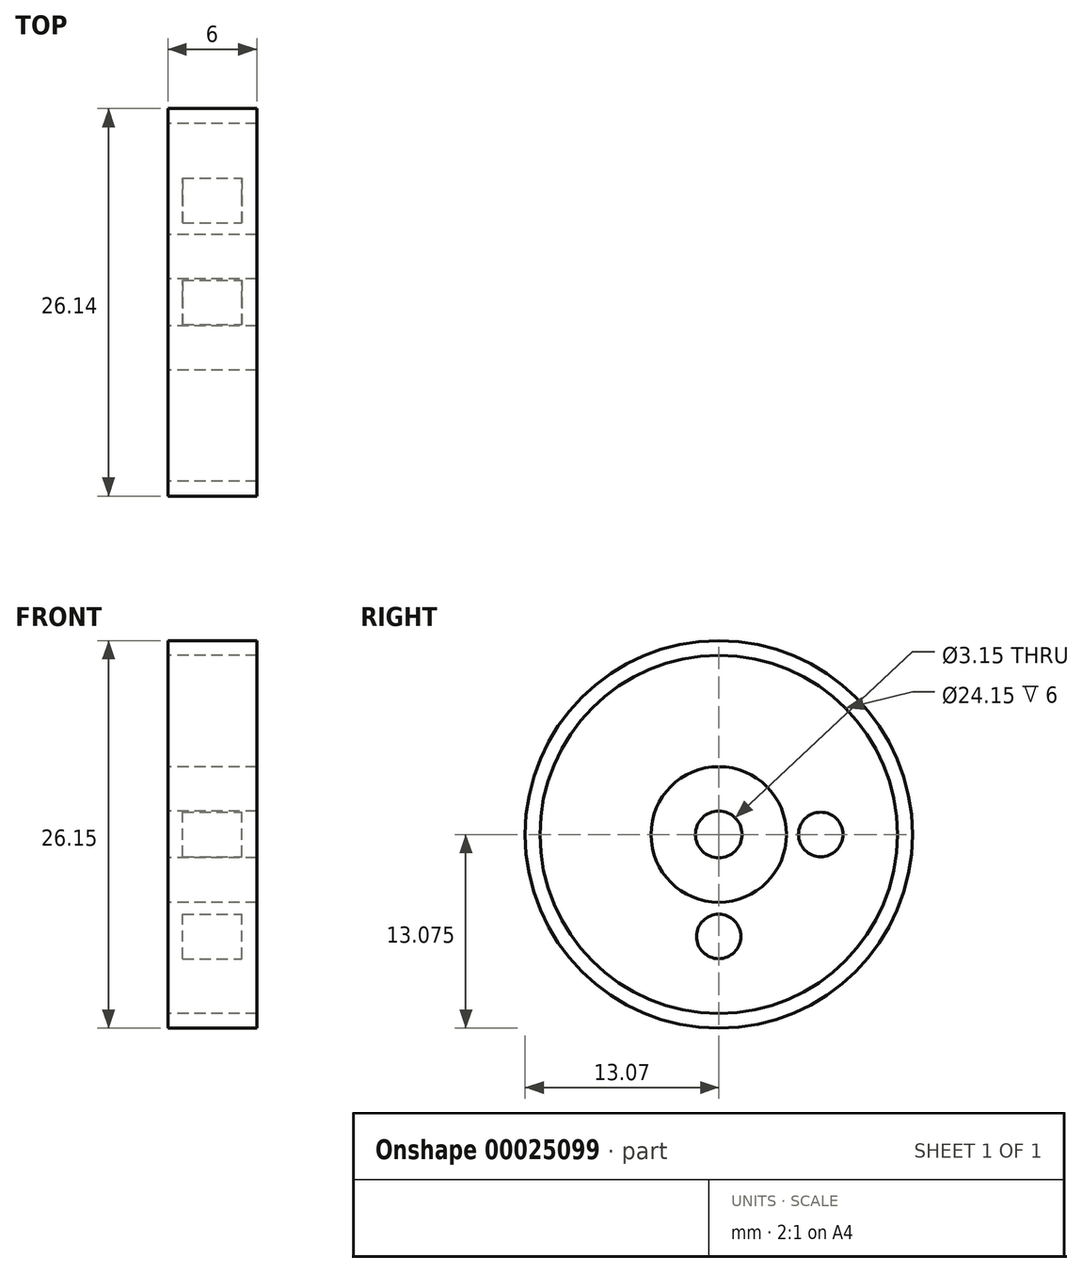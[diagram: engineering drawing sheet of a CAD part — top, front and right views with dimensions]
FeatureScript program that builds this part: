
annotation { "Feature Type Name" : "Feature", "Feature Type Description" : "" }
export const myFeature = defineFeature(function(context is Context, id is Id, definition is map)
    precondition{}
    {
        {
            var Q0;
            Q0=qCreatedBy(makeId("Front.planeOp"),FACE);
            var sketch = newSketch(context, id + "F0", { "sketchPlane" : qUnion([Q0])});
            skLineSegment(sketch, "E0.bottom", {"start": v(-0.12, 1.48) * mm, "end": v(0.88, 1.48) * mm});
            skLineSegment(sketch, "E0.top", {"start": v(-0.12, -1.52) * mm, "end": v(5.88, -1.52) * mm});
            skLineSegment(sketch, "E0.left", {"start": v(-0.12, 1.48) * mm, "end": v(-0.12, -1.52) * mm});
            skLineSegment(sketch, "E0.right", {"start": v(5.88, 1.48) * mm, "end": v(5.88, -1.52) * mm});
            skLineSegment(sketch, "E1.left", {"start": v(0.88, 8.98) * mm, "end": v(0.88, 1.48) * mm});
            skLineSegment(sketch, "E1.right", {"start": v(4.88, 8.98) * mm, "end": v(4.88, 1.48) * mm});
            skLineSegment(sketch, "E2.trimOffspring", {"start": v(4.88, 1.48) * mm, "end": v(5.88, 1.48) * mm});
            skLineSegment(sketch, "E3", {"start": v(-11.4, -3.1) * mm, "end": v(19.97, -3.1) * mm, "construction": true});
            skLineSegment(sketch, "E4.bottom", {"start": v(5.88, 9.98) * mm, "end": v(-0.12, 9.98) * mm});
            skLineSegment(sketch, "E4.top", {"start": v(5.88, 8.98) * mm, "end": v(4.88, 8.98) * mm});
            skLineSegment(sketch, "E4.left", {"start": v(5.88, 9.98) * mm, "end": v(5.88, 8.98) * mm});
            skLineSegment(sketch, "E4.right", {"start": v(-0.12, 9.98) * mm, "end": v(-0.12, 8.98) * mm});
            skLineSegment(sketch, "E5.trimOffspring", {"start": v(0.88, 8.98) * mm, "end": v(-0.12, 8.98) * mm});
            skSolve(sketch);
        }
        {
            var Q0;
            Q0 = qSketchRegion(id + "F0", true);
            var Q1;
            Q1=sQuery(id+"F0.wireOp",EDGE,"E3");
            revolve(context, id + "F1", {"entities" : qUnion([Q0]), "axis" : qUnion([Q1]), "revolveType" : RevolveType.FULL});
        }
        {
            var Q0;
            Q0=makeQuery(id+"F1.opRevolve","SWEPT_FACE",FACE,{"disambiguationData":[OSD([sQuery(id+"F0.wireOp",EDGE,"E1.right")])]});
            var sketch = newSketch(context, id + "F2", { "sketchPlane" : qUnion([Q0])});
            skCircle(sketch, "E6", {"center": v(0, -3.1) * mm, "radius": 6.88 * mm});
            skCircle(sketch, "E7", {"center": v(0, -9.98) * mm, "radius": 1.5 * mm});
            skCircle(sketch, "E8.1.0", {"center": v(4.87, -7.96) * mm, "radius": 1.5 * mm});
            skCircle(sketch, "E8.2.0", {"center": v(6.88, -3.1) * mm, "radius": 1.5 * mm});
            skCircle(sketch, "E8.3.0", {"center": v(4.87, 1.77) * mm, "radius": 1.5 * mm});
            skCircle(sketch, "E8.4.0", {"center": v(0, 3.79) * mm, "radius": 1.5 * mm});
            skCircle(sketch, "E8.5.0", {"center": v(-4.87, 1.77) * mm, "radius": 1.5 * mm});
            skCircle(sketch, "E8.6.0", {"center": v(-6.88, -3.1) * mm, "radius": 1.5 * mm});
            skCircle(sketch, "E8.7.0", {"center": v(-4.87, -7.96) * mm, "radius": 1.5 * mm});
            skSolve(sketch);
        }
        {
            var Q0;
            {var subQ0=sQuery(id+"F2.wireOp",EDGE,"E8.5.0");var subQ1=sQuery(id+"F2.wireOp",EDGE,"E6");var subQ3=makeQuery(id+"F2.imprint","INTERSECT",VERTEX,{"disambiguationData":[OD(0.0)],"derivedFrom":[subQ1,subQ0]});Q0=makeQuery(id+"F2.imprint","IMPRINT",FACE,{"disambiguationData":[TD([[makeQuery(id+"F2.imprint","IMPRINT",EDGE,{"disambiguationData":[TD([[subQ3,-1.0]])],"derivedFrom":subQ1}),1.0]])]});}
            var Q1;
            {var subQ0=sQuery(id+"F2.wireOp",EDGE,"E8.5.0");var subQ1=sQuery(id+"F2.wireOp",EDGE,"E6");var subQ3=makeQuery(id+"F2.imprint","INTERSECT",VERTEX,{"disambiguationData":[OD(0.0)],"derivedFrom":[subQ1,subQ0]});Q1=makeQuery(id+"F2.imprint","IMPRINT",FACE,{"disambiguationData":[TD([[makeQuery(id+"F2.imprint","IMPRINT",EDGE,{"disambiguationData":[TD([[subQ3,-1.0]])],"derivedFrom":subQ1}),-1.0]])]});}
            var Q2;
            {var subQ0=sQuery(id+"F2.wireOp",EDGE,"E8.6.0");var subQ1=sQuery(id+"F2.wireOp",EDGE,"E6");var subQ3=makeQuery(id+"F2.imprint","INTERSECT",VERTEX,{"disambiguationData":[OD(0.0)],"derivedFrom":[subQ1,subQ0]});Q2=makeQuery(id+"F2.imprint","IMPRINT",FACE,{"disambiguationData":[TD([[makeQuery(id+"F2.imprint","IMPRINT",EDGE,{"disambiguationData":[TD([[subQ3,-1.0]])],"derivedFrom":subQ1}),1.0]])]});}
            var Q3;
            {var subQ0=sQuery(id+"F2.wireOp",EDGE,"E8.6.0");var subQ1=sQuery(id+"F2.wireOp",EDGE,"E6");var subQ3=makeQuery(id+"F2.imprint","INTERSECT",VERTEX,{"disambiguationData":[OD(0.0)],"derivedFrom":[subQ1,subQ0]});Q3=makeQuery(id+"F2.imprint","IMPRINT",FACE,{"disambiguationData":[TD([[makeQuery(id+"F2.imprint","IMPRINT",EDGE,{"disambiguationData":[TD([[subQ3,-1.0]])],"derivedFrom":subQ1}),-1.0]])]});}
            var Q4;
            {var subQ0=sQuery(id+"F2.wireOp",EDGE,"E8.7.0");var subQ1=sQuery(id+"F2.wireOp",EDGE,"E6");var subQ3=makeQuery(id+"F2.imprint","INTERSECT",VERTEX,{"disambiguationData":[OD(0.0)],"derivedFrom":[subQ1,subQ0]});Q4=makeQuery(id+"F2.imprint","IMPRINT",FACE,{"disambiguationData":[TD([[makeQuery(id+"F2.imprint","IMPRINT",EDGE,{"disambiguationData":[TD([[subQ3,-1.0]])],"derivedFrom":subQ1}),1.0]])]});}
            var Q5;
            {var subQ0=sQuery(id+"F2.wireOp",EDGE,"E8.7.0");var subQ1=sQuery(id+"F2.wireOp",EDGE,"E6");var subQ3=makeQuery(id+"F2.imprint","INTERSECT",VERTEX,{"disambiguationData":[OD(0.0)],"derivedFrom":[subQ1,subQ0]});Q5=makeQuery(id+"F2.imprint","IMPRINT",FACE,{"disambiguationData":[TD([[makeQuery(id+"F2.imprint","IMPRINT",EDGE,{"disambiguationData":[TD([[subQ3,-1.0]])],"derivedFrom":subQ1}),-1.0]])]});}
            var Q6;
            {var subQ0=sQuery(id+"F2.wireOp",EDGE,"E7");var subQ1=sQuery(id+"F2.wireOp",EDGE,"E6");var subQ3=makeQuery(id+"F2.imprint","INTERSECT",VERTEX,{"disambiguationData":[OD(0.0)],"derivedFrom":[subQ1,subQ0]});Q6=makeQuery(id+"F2.imprint","IMPRINT",FACE,{"disambiguationData":[TD([[makeQuery(id+"F2.imprint","IMPRINT",EDGE,{"disambiguationData":[TD([[subQ3,-1.0]])],"derivedFrom":subQ1}),1.0]])]});}
            var Q7;
            {var subQ0=sQuery(id+"F2.wireOp",EDGE,"E7");var subQ1=sQuery(id+"F2.wireOp",EDGE,"E6");var subQ3=makeQuery(id+"F2.imprint","INTERSECT",VERTEX,{"disambiguationData":[OD(0.0)],"derivedFrom":[subQ1,subQ0]});Q7=makeQuery(id+"F2.imprint","IMPRINT",FACE,{"disambiguationData":[TD([[makeQuery(id+"F2.imprint","IMPRINT",EDGE,{"disambiguationData":[TD([[subQ3,-1.0]])],"derivedFrom":subQ1}),-1.0]])]});}
            var Q8;
            {var subQ0=sQuery(id+"F2.wireOp",EDGE,"E8.1.0");var subQ1=sQuery(id+"F2.wireOp",EDGE,"E6");var subQ3=makeQuery(id+"F2.imprint","INTERSECT",VERTEX,{"disambiguationData":[OD(0.0)],"derivedFrom":[subQ1,subQ0]});Q8=makeQuery(id+"F2.imprint","IMPRINT",FACE,{"disambiguationData":[TD([[makeQuery(id+"F2.imprint","IMPRINT",EDGE,{"disambiguationData":[TD([[subQ3,-1.0]])],"derivedFrom":subQ1}),1.0]])]});}
            var Q9;
            {var subQ0=sQuery(id+"F2.wireOp",EDGE,"E8.1.0");var subQ1=sQuery(id+"F2.wireOp",EDGE,"E6");var subQ3=makeQuery(id+"F2.imprint","INTERSECT",VERTEX,{"disambiguationData":[OD(0.0)],"derivedFrom":[subQ1,subQ0]});Q9=makeQuery(id+"F2.imprint","IMPRINT",FACE,{"disambiguationData":[TD([[makeQuery(id+"F2.imprint","IMPRINT",EDGE,{"disambiguationData":[TD([[subQ3,-1.0]])],"derivedFrom":subQ1}),-1.0]])]});}
            var Q10;
            {var subQ0=sQuery(id+"F2.wireOp",EDGE,"E8.2.0");var subQ1=sQuery(id+"F2.wireOp",EDGE,"E6");var subQ3=makeQuery(id+"F2.imprint","INTERSECT",VERTEX,{"disambiguationData":[OD(0.0)],"derivedFrom":[subQ1,subQ0]});Q10=makeQuery(id+"F2.imprint","IMPRINT",FACE,{"disambiguationData":[TD([[makeQuery(id+"F2.imprint","IMPRINT",EDGE,{"disambiguationData":[TD([[subQ3,1.0]])],"derivedFrom":subQ1}),1.0]])]});}
            var Q11;
            {var subQ0=sQuery(id+"F2.wireOp",EDGE,"E8.2.0");var subQ1=sQuery(id+"F2.wireOp",EDGE,"E6");var subQ3=makeQuery(id+"F2.imprint","INTERSECT",VERTEX,{"disambiguationData":[OD(0.0)],"derivedFrom":[subQ1,subQ0]});Q11=makeQuery(id+"F2.imprint","IMPRINT",FACE,{"disambiguationData":[TD([[makeQuery(id+"F2.imprint","IMPRINT",EDGE,{"disambiguationData":[TD([[subQ3,1.0]])],"derivedFrom":subQ1}),-1.0]])]});}
            var Q12;
            {var subQ0=sQuery(id+"F2.wireOp",EDGE,"E8.3.0");var subQ1=sQuery(id+"F2.wireOp",EDGE,"E6");var subQ3=makeQuery(id+"F2.imprint","INTERSECT",VERTEX,{"disambiguationData":[OD(0.0)],"derivedFrom":[subQ1,subQ0]});Q12=makeQuery(id+"F2.imprint","IMPRINT",FACE,{"disambiguationData":[TD([[makeQuery(id+"F2.imprint","IMPRINT",EDGE,{"disambiguationData":[TD([[subQ3,-1.0]])],"derivedFrom":subQ1}),1.0]])]});}
            var Q13;
            {var subQ0=sQuery(id+"F2.wireOp",EDGE,"E8.3.0");var subQ1=sQuery(id+"F2.wireOp",EDGE,"E6");var subQ3=makeQuery(id+"F2.imprint","INTERSECT",VERTEX,{"disambiguationData":[OD(0.0)],"derivedFrom":[subQ1,subQ0]});Q13=makeQuery(id+"F2.imprint","IMPRINT",FACE,{"disambiguationData":[TD([[makeQuery(id+"F2.imprint","IMPRINT",EDGE,{"disambiguationData":[TD([[subQ3,-1.0]])],"derivedFrom":subQ1}),-1.0]])]});}
            var Q14;
            {var subQ0=sQuery(id+"F2.wireOp",EDGE,"E8.4.0");var subQ1=sQuery(id+"F2.wireOp",EDGE,"E6");var subQ3=makeQuery(id+"F2.imprint","INTERSECT",VERTEX,{"disambiguationData":[OD(0.0)],"derivedFrom":[subQ1,subQ0]});Q14=makeQuery(id+"F2.imprint","IMPRINT",FACE,{"disambiguationData":[TD([[makeQuery(id+"F2.imprint","IMPRINT",EDGE,{"disambiguationData":[TD([[subQ3,-1.0]])],"derivedFrom":subQ1}),1.0]])]});}
            var Q15;
            {var subQ0=sQuery(id+"F2.wireOp",EDGE,"E8.4.0");var subQ1=sQuery(id+"F2.wireOp",EDGE,"E6");var subQ3=makeQuery(id+"F2.imprint","INTERSECT",VERTEX,{"disambiguationData":[OD(0.0)],"derivedFrom":[subQ1,subQ0]});Q15=makeQuery(id+"F2.imprint","IMPRINT",FACE,{"disambiguationData":[TD([[makeQuery(id+"F2.imprint","IMPRINT",EDGE,{"disambiguationData":[TD([[subQ3,-1.0]])],"derivedFrom":subQ1}),-1.0]])]});}
            extrude(context, id + "F3", {"entities" : qUnion([Q0, Q1, Q2, Q3, Q4, Q5, Q6, Q7, Q8, Q9, Q10, Q11, Q12, Q13, Q14, Q15]), "operationType" : NewBodyOperationType.REMOVE, "endBound" : BoundingType.THROUGH_ALL, "oppositeDirection" : true, "depth" : 25 * mm});
        }
    });
